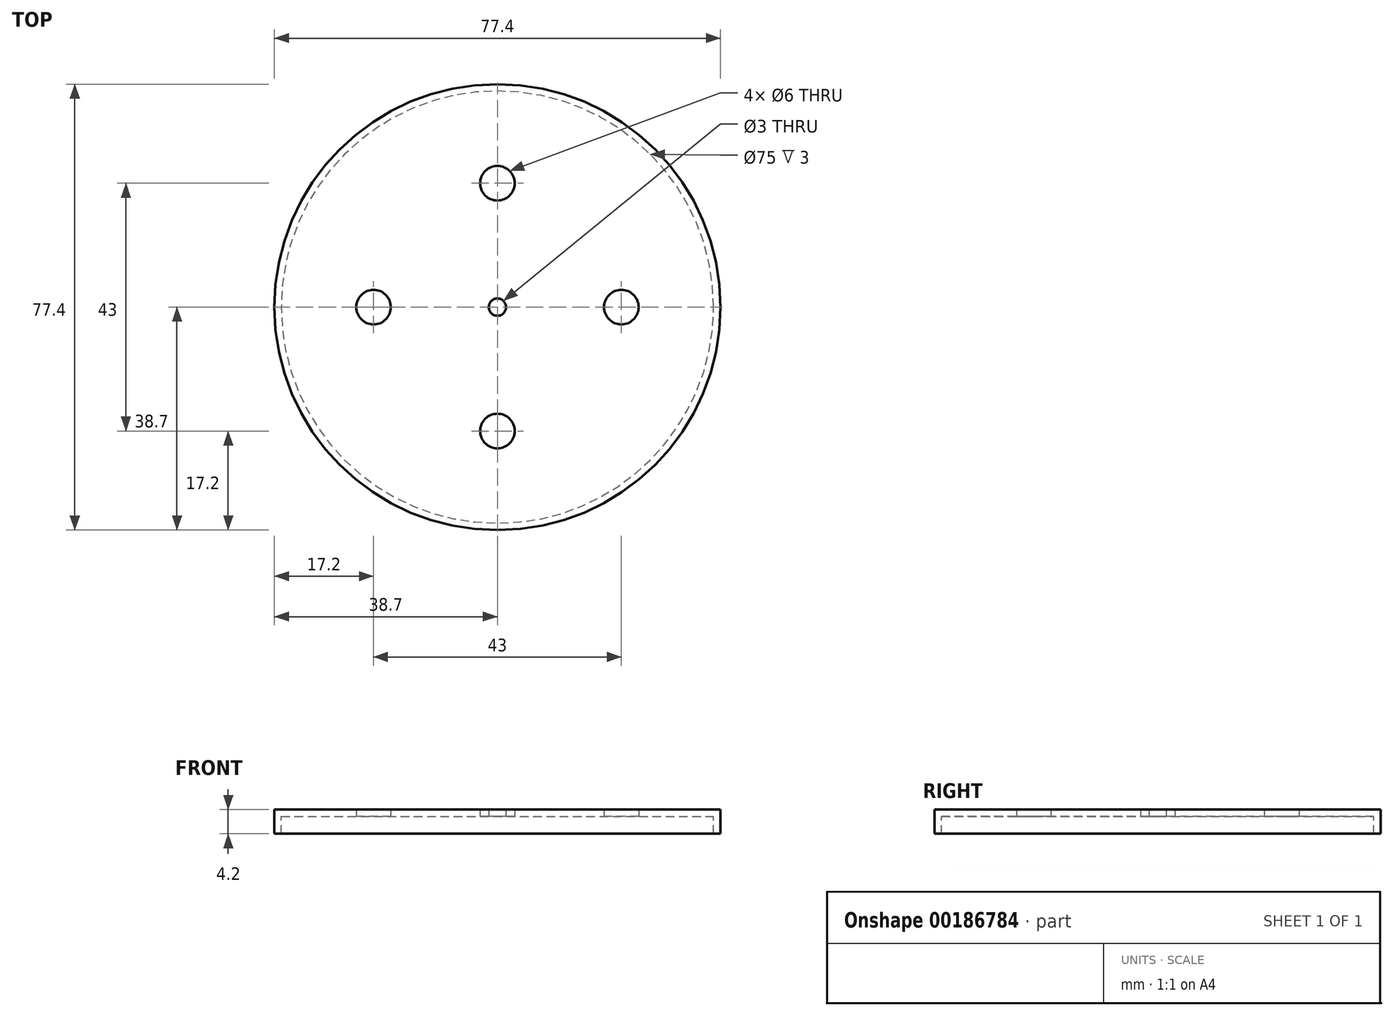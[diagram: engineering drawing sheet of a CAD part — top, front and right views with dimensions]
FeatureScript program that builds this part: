
annotation { "Feature Type Name" : "Feature", "Feature Type Description" : "" }
export const myFeature = defineFeature(function(context is Context, id is Id, definition is map)
    precondition{}
    {
        {
            var Q0;
            Q0=qCreatedBy(makeId("Top.planeOp"),FACE);
            var sketch = newSketch(context, id + "F0", { "sketchPlane" : qUnion([Q0])});
            skCircle(sketch, "E0", {"center": v(0, 0) * mm, "radius": 38.7 * mm});
            skLineSegment(sketch, "E1", {"start": v(-38.7, 0) * mm, "end": v(38.7, 0) * mm, "construction": true});
            skLineSegment(sketch, "E2", {"start": v(0, 38.7) * mm, "end": v(0, -38.7) * mm, "construction": true});
            skCircle(sketch, "E3", {"center": v(0, 21.5) * mm, "radius": 3 * mm});
            skCircle(sketch, "E4.MirrorC", {"center": v(0, -21.5) * mm, "radius": 3 * mm});
            skCircle(sketch, "E5", {"center": v(0, 0) * mm, "radius": 1.5 * mm});
            skCircle(sketch, "E6", {"center": v(-21.5, 0) * mm, "radius": 3 * mm});
            skCircle(sketch, "E7", {"center": v(21.5, 0) * mm, "radius": 3 * mm});
            skSolve(sketch);
        }
        {
            var Q0;
            Q0=qSketchRegion(id+"F0",true);
            extrude(context, id + "F1", {"entities" : qUnion([Q0]), "depth" : 1.2 * mm, "offsetDistance" : 25 * mm});
        }
        {
            var Q0;
            Q0=makeQuery(id+"F1.opExtrude","CAP_FACE",FACE,{"disambiguationData":[OSD([sQuery(id+"F0.wireOp",EDGE,"E0"),sQuery(id+"F0.wireOp",EDGE,"E3"),sQuery(id+"F0.wireOp",EDGE,"E4.MirrorC"),sQuery(id+"F0.wireOp",EDGE,"E5"),sQuery(id+"F0.wireOp",EDGE,"E6"),sQuery(id+"F0.wireOp",EDGE,"E7")])],"isStart":true});
            var sketch = newSketch(context, id + "F2", { "sketchPlane" : qUnion([Q0])});
            skCircle(sketch, "E8.0", {"center": v(0, 0) * mm, "radius": 38.7 * mm});
            skCircle(sketch, "E9.0", {"center": v(0, 0) * mm, "radius": 37.5 * mm});
            skSolve(sketch);
        }
        {
            var Q0;
            Q0 = qSketchRegion(id + "F2", true);
            extrude(context, id + "F3", {"entities" : qUnion([Q0]), "operationType" : NewBodyOperationType.ADD, "depth" : 3 * mm, "offsetDistance" : 25 * mm});
        }
    });
